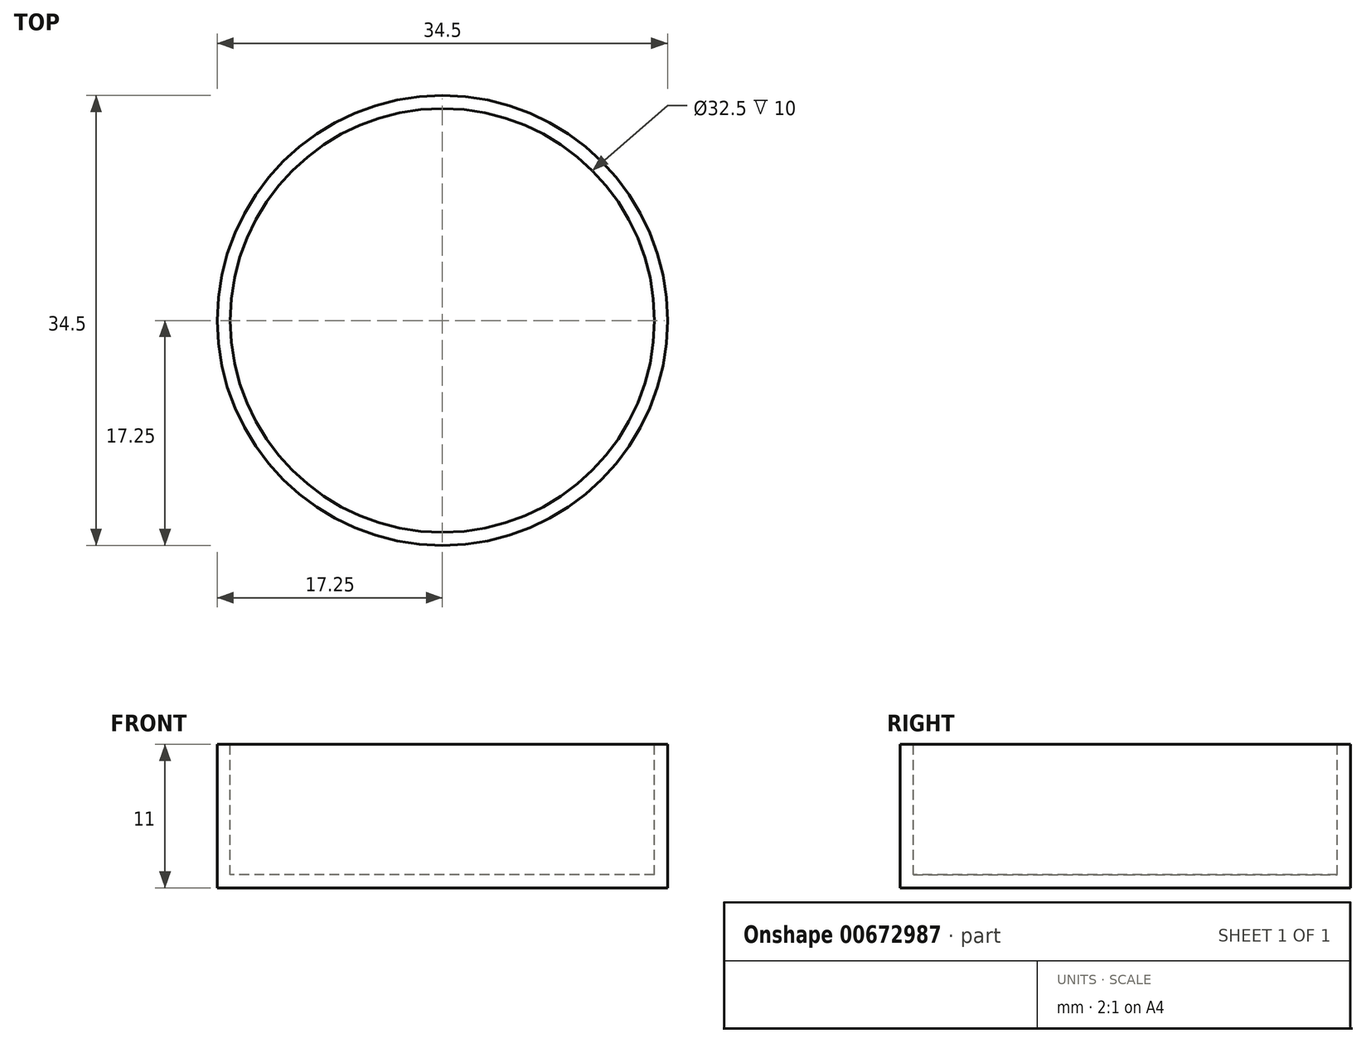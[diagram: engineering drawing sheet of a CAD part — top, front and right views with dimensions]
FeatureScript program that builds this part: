
annotation { "Feature Type Name" : "Feature", "Feature Type Description" : "" }
export const myFeature = defineFeature(function(context is Context, id is Id, definition is map)
    precondition{}
    {
        {
            var Q0;
            Q0=qCreatedBy(makeId("Top.planeOp"),FACE);
            var sketch = newSketch(context, id + "F0", { "sketchPlane" : qUnion([Q0])});
            skCircle(sketch, "E0", {"center": v(0, 0) * mm, "radius": 17.25 * mm});
            skSolve(sketch);
        }
        {
            var Q0;
            Q0=makeQuery(id+"F0.imprint","IMPRINT",FACE,{"disambiguationData":[TD([[makeQuery(id+"F0.imprint","IMPRINT",EDGE,{"derivedFrom":sQuery(id+"F0.wireOp",EDGE,"E0")}),1.0]])]});
            extrude(context, id + "F1", {"entities" : qUnion([Q0]), "depth" : 11 * mm, "offsetDistance" : 25 * mm});
        }
        {
            var Q0;
            Q0=makeQuery(id+"F1.opExtrude","CAP_FACE",FACE,{"disambiguationData":[OSD([sQuery(id+"F0.wireOp",EDGE,"E0")])],"isStart":false});
            var sketch = newSketch(context, id + "F2", { "sketchPlane" : qUnion([Q0])});
            skCircle(sketch, "E1", {"center": v(0, 0) * mm, "radius": 16.25 * mm});
            skSolve(sketch);
        }
        {
            var Q0;
            Q0=makeQuery(id+"F2.imprint","IMPRINT",FACE,{"disambiguationData":[TD([[makeQuery(id+"F2.imprint","IMPRINT",EDGE,{"derivedFrom":sQuery(id+"F2.wireOp",EDGE,"E1")}),1.0]])]});
            var Q1;
            Q1 = qSketchRegion(id + "F0", true);
            extrude(context, id + "F3", {"entities" : qUnion([Q0, Q1]), "operationType" : NewBodyOperationType.REMOVE, "oppositeDirection" : true, "depth" : 10 * mm, "offsetDistance" : 25 * mm});
        }
    });
